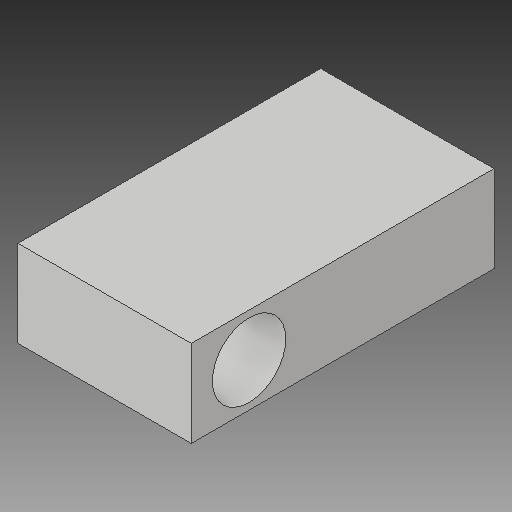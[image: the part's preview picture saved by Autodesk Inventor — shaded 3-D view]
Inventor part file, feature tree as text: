
AUTODESK INVENTOR PART (.ipt)
format: ipt  version: 2019 (Build 230136000, 136)  size: 99,328 bytes
history: native  units: mm
features: sketch x2, extrude x1, hole x1
ambient origin geometry x8: Origin, YZ Plane, XZ Plane, XY Plane, X Axis, Y Axis, Z Axis, Center Point
bodies: Solid1 (feature_tree)
feature tree (4):
  extrude  "Extrusion1"  Depth=75.0mm
  hole  "Hole1"  [1 undecoded]
  sketch  "Sketch1"  dims[d0=150.0mm d1=75.0mm]
  sketch  "Sketch2"  dims[d2=262.0mm d3=0.0mm d4=50.0mm d5=37.5mm d6=63.5mm d7=6.0mm d8=4.0mm d9=2.0mm d10=90.0deg d11=8.0mm d12=20.594885mm]
note: 1 required parameter value undecoded (feature->parameter linkage not recoverable at this tier; creation-order binding heuristic only, values carry confidence <= 0.55)
